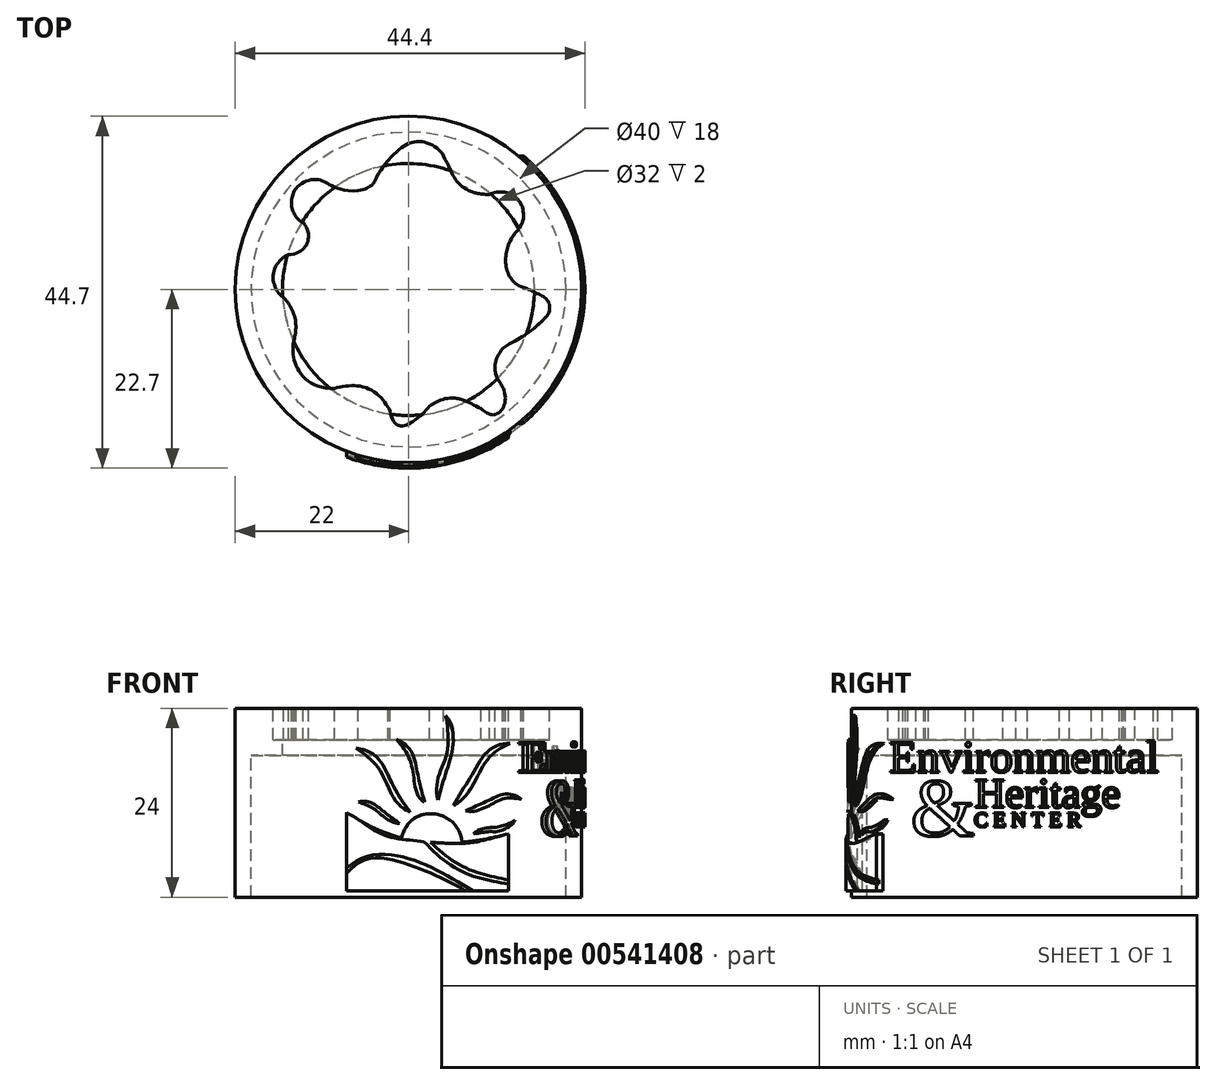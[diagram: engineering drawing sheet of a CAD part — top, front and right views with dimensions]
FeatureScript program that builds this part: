
annotation { "Feature Type Name" : "Feature", "Feature Type Description" : "" }
export const myFeature = defineFeature(function(context is Context, id is Id, definition is map)
    precondition{}
    {
        {
            var Q0;
            Q0=qCreatedBy(makeId("Top.planeOp"),FACE);
            var Q1;
            Q1=qBodyType(qCreatedBy(id+"F1",EDGE),BodyType.WIRE);
            cPlane(context, id + "F0", {"entities" : qUnion([Q0, Q1]), "cplaneType" : CPlaneType.OFFSET, "offset" : 12 * mm, "width" : 150 * mm, "height" : 150 * mm});
        }
        {
            var Q0;
            Q0=qCreatedBy(id+"F0.planeOp",FACE);
            var sketch = newSketch(context, id + "F1", { "sketchPlane" : qUnion([Q0])});
            skCircle(sketch, "E0", {"center": v(0, 0) * mm, "radius": 22 * mm});
            skFitSpline(sketch, "E1", {"points": [v(-14.3, 12.84) * mm, v(-11.44, 13.95) * mm, v(-6.4, 12.53) * mm], "startDerivative": vector(4.46, 5.6) * mm, "endDerivative": vector(16.32, 0.58) * mm});
            skFitSpline(sketch, "E2", {"points": [v(-14.3, 12.84) * mm, v(-14.8, 10.36) * mm, v(-13.38, 8.48) * mm], "startDerivative": vector(-2.91, -3.74) * mm, "endDerivative": vector(4.44, -2.3) * mm});
            skFitSpline(sketch, "E3", {"points": [v(-13.38, 8.48) * mm, v(-12.7, 6.62) * mm, v(-15.26, 4.45) * mm], "startDerivative": vector(2.5, -2.67) * mm, "endDerivative": vector(-9.07, 0.1) * mm});
            skFitSpline(sketch, "E4", {"points": [v(-15.26, 4.45) * mm, v(-17.17, 1.96) * mm, v(-15.87, -1.05) * mm], "startDerivative": vector(-5.88, -2.54) * mm, "endDerivative": vector(5.37, -3.99) * mm});
            skFitSpline(sketch, "E5", {"points": [v(-15.87, -1.05) * mm, v(-14.36, -3.98) * mm, v(-14.54, -6.45) * mm], "startDerivative": vector(4.6, -4.23) * mm, "endDerivative": vector(-1.12, -5.28) * mm});
            skFitSpline(sketch, "E6", {"points": [v(-14.54, -6.45) * mm, v(-14.3, -9.6) * mm, v(-9.38, -12.57) * mm], "startDerivative": vector(-1.49, -4.88) * mm, "endDerivative": vector(14.07, 0.6) * mm});
            skFitSpline(sketch, "E7", {"points": [v(-9.38, -12.57) * mm, v(-5.16, -12.57) * mm, v(-2.36, -15.43) * mm], "startDerivative": vector(7.18, 2.12) * mm, "endDerivative": vector(2.53, -6.19) * mm});
            skFitSpline(sketch, "E8", {"points": [v(-2.36, -15.43) * mm, v(-0.75, -17.32) * mm, v(2.7, -14.82) * mm], "startDerivative": vector(1.67, -9.42) * mm, "endDerivative": vector(5.03, 5.85) * mm});
            skFitSpline(sketch, "E9", {"points": [v(2.7, -14.82) * mm, v(5.45, -13.78) * mm, v(9.22, -15.14) * mm], "startDerivative": vector(4.06, 3.24) * mm, "endDerivative": vector(7.18, -3.93) * mm});
            skFitSpline(sketch, "E10", {"points": [v(9.22, -15.14) * mm, v(11.11, -15.85) * mm, v(12.13, -12.78) * mm], "startDerivative": vector(4.38, -3.77) * mm, "endDerivative": vector(-2.9, 8.35) * mm});
            skFitSpline(sketch, "E11", {"points": [v(12.13, -12.78) * mm, v(11.06, -10.66) * mm, v(11.96, -7.51) * mm], "startDerivative": vector(-1.65, 4.16) * mm, "endDerivative": vector(4.57, 5.25) * mm});
            skFitSpline(sketch, "E12", {"points": [v(11.96, -7.51) * mm, v(14.65, -5.88) * mm, v(17.91, -2.7) * mm], "startDerivative": vector(3.62, 3.57) * mm, "endDerivative": vector(-0.15, 3.1) * mm});
            skFitSpline(sketch, "E13", {"points": [v(17.91, -2.7) * mm, v(16.74, -0.7) * mm, v(14.28, 0.37) * mm], "startDerivative": vector(0.98, 7.59) * mm, "endDerivative": vector(-4.1, 1.2) * mm});
            skFitSpline(sketch, "E14", {"points": [v(14.28, 0.37) * mm, v(12.43, 2.83) * mm, v(12.74, 5.73) * mm], "startDerivative": vector(-6.41, 2.8) * mm, "endDerivative": vector(2.08, 5.38) * mm});
            skFitSpline(sketch, "E15", {"points": [v(12.74, 5.73) * mm, v(14.05, 7.73) * mm, v(14.57, 9.89) * mm], "startDerivative": vector(4.72, 10.1) * mm, "endDerivative": vector(-1.17, 4.74) * mm});
            skFitSpline(sketch, "E16", {"points": [v(14.57, 9.89) * mm, v(13.17, 12.02) * mm, v(10.32, 12.08) * mm], "startDerivative": vector(0.08, 3.85) * mm, "endDerivative": vector(-4.12, -2.28) * mm});
            skFitSpline(sketch, "E17", {"points": [v(10.32, 12.08) * mm, v(6.46, 13.4) * mm, v(4.44, 16.97) * mm], "startDerivative": vector(-9.93, -0.41) * mm, "endDerivative": vector(-5.62, 10.83) * mm});
            skFitSpline(sketch, "E18", {"points": [v(4.44, 16.97) * mm, v(1.52, 18.8) * mm, v(-2.58, 16.4) * mm], "startDerivative": vector(-2.9, 6.35) * mm, "endDerivative": vector(-8.38, -9.56) * mm});
            skFitSpline(sketch, "E19", {"points": [v(-2.58, 16.4) * mm, v(-4.36, 13.61) * mm, v(-6.4, 12.53) * mm], "startDerivative": vector(-9.43, -11.95) * mm, "endDerivative": vector(-8.2, -1.4) * mm});
            skCircle(sketch, "E20", {"center": v(0, 0) * mm, "radius": 20 * mm});
            skSolve(sketch);
        }
        {
            var Q0;
            Q0=qCreatedBy(makeId("Top.planeOp"),FACE);
            cPlane(context, id + "F2", {"entities" : qUnion([Q0]), "cplaneType" : CPlaneType.OFFSET, "offset" : 8 * mm, "width" : 150 * mm, "height" : 150 * mm});
        }
        {
            var Q0;
            Q0=qCreatedBy(id+"F2.planeOp",FACE);
            var sketch = newSketch(context, id + "F3", { "sketchPlane" : qUnion([Q0])});
            skCircle(sketch, "E21", {"center": v(0, 0) * mm, "radius": 20 * mm});
            skCircle(sketch, "E22", {"center": v(0, 0) * mm, "radius": 16 * mm});
            skSolve(sketch);
        }
        {
            var Q0;
            Q0=makeQuery(id+"F1.imprint","IMPRINT",FACE,{"disambiguationData":[TD([[makeQuery(id+"F1.imprint","IMPRINT",EDGE,{"derivedFrom":sQuery(id+"F1.wireOp",EDGE,"E1")}),1.0]])]});
            extrude(context, id + "F4", {"entities" : qUnion([Q0]), "oppositeDirection" : true, "depth" : 4 * mm});
        }
        {
            var Q0;
            Q0=makeQuery(id+"F1.imprint","IMPRINT",FACE,{"disambiguationData":[TD([[makeQuery(id+"F1.imprint","IMPRINT",EDGE,{"derivedFrom":sQuery(id+"F1.wireOp",EDGE,"E0")}),1.0]])]});
            extrude(context, id + "F5", {"entities" : qUnion([Q0]), "operationType" : NewBodyOperationType.ADD, "oppositeDirection" : true, "depth" : 24 * mm});
        }
        {
            var Q0;
            Q0=makeQuery(id+"F3.imprint","IMPRINT",FACE,{"disambiguationData":[TD([[makeQuery(id+"F3.imprint","IMPRINT",EDGE,{"derivedFrom":sQuery(id+"F3.wireOp",EDGE,"E21")}),1.0]])]});
            extrude(context, id + "F6", {"entities" : qUnion([Q0]), "operationType" : NewBodyOperationType.ADD, "oppositeDirection" : true, "depth" : 2 * mm});
        }
        {
            var Q0;
            Q0=qCreatedBy(id+"F0.planeOp",FACE);
            var sketch = newSketch(context, id + "F7", { "sketchPlane" : qUnion([Q0])});
            skCircle(sketch, "E23", {"center": v(0, 0) * mm, "radius": 22.4 * mm});
            skSolve(sketch);
        }
        {
            var Q0;
            Q0=qSketchRegion(id+"F7",true);
            var Q1;
            Q1=qConstructionFilter(qBodyType(qCreatedBy(id+"F7",EDGE),BodyType.WIRE),ConstructionObject.NO);
            extrude(context, id + "F8", {"entities" : qUnion([Q0]), "bodyType" : ToolBodyType.SURFACE, "operationType" : NewBodyOperationType.ADD, "surfaceEntities" : qUnion([Q1]), "oppositeDirection" : true, "depth" : 24 * mm});
        }
        {
            var Q0;
            Q0=qCreatedBy(makeId("Right.planeOp"),FACE);
            var sketch = newSketch(context, id + "F9", { "sketchPlane" : qUnion([Q0])});
            skText(sketch, "E24", { "text": "Environmental", "fontName": "Tinos-Regular.ttf"});
            skText(sketch, "E25", { "text": "Heritage", "fontName": "Tinos-Regular.ttf"});
            skText(sketch, "E26", { "text": "C E N T E R", "fontName": "Tinos-Regular.ttf"});
            skText(sketch, "E27", { "text": "&", "fontName": "Tinos-Regular.ttf"});
            const initialGuessF9  = {"E24": [-0.01718, 0.00388, 1, 0, 0.00415], "E25": [-0.00635, -0.0006, 1, 0, 0.00388], "E26": [-0.00638, -0.00305, 1, 0, 0.0019], "E27": [-0.01444, -0.0042, 1, 0, 0.00757]};
            skSetInitialGuess(sketch, initialGuessF9);
            skSolve(sketch);
        }
        {
            var Q0;
            Q0=qSketchRegion(id+"F9",true);
            var Q1;
            Q1=makeQuery(id+"F8.opExtrude","SWEPT_FACE",FACE,{"disambiguationData":[OSD([sQuery(id+"F7.wireOp",EDGE,"E23")])]});
            var Q2;
            Q2=makeQuery(id+"F5.opExtrude","SWEPT_FACE",FACE,{"disambiguationData":[OSD([sQuery(id+"F1.wireOp",EDGE,"E0")])]});
            extrude(context, id + "F10", {"entities" : qUnion([Q0]), "operationType" : NewBodyOperationType.ADD, "endBound" : BoundingType.UP_TO_SURFACE, "endBoundEntityFace" : qUnion([Q1]), "depth" : 25 * mm, "hasSecondDirection" : true, "secondDirectionBound" : SecondDirectionBoundingType.UP_TO_SURFACE, "secondDirectionOppositeDirection" : false, "secondDirectionBoundEntityFace" : qUnion([Q2]), "secondDirectionDepth" : 25 * mm, "offsetDistance" : 25 * mm});
        }
        {
            var Q0;
            Q0=qCreatedBy(makeId("Front.planeOp"),FACE);
            var sketch = newSketch(context, id + "F11", { "sketchPlane" : qUnion([Q0])});
            skFitSpline(sketch, "E28", {"points": [v(4.72, 11.1) * mm, v(5.15, 5) * mm, v(3.74, 0.35) * mm], "startDerivative": vector(9.25, -10.85) * mm, "endDerivative": vector(-6.86, -24.58) * mm});
            skFitSpline(sketch, "E29", {"points": [v(4.72, 11.1) * mm, v(4.41, 4.9) * mm, v(3.74, 0.35) * mm], "startDerivative": vector(3.34, -19.7) * mm, "endDerivative": vector(3.13, -13.42) * mm});
            skFitSpline(sketch, "E30", {"points": [v(-1.5, 8.04) * mm, v(1.02, 4.33) * mm, v(2.06, 0.08) * mm], "startDerivative": vector(12.14, -4.86) * mm, "endDerivative": vector(3.6, -12.42) * mm});
            skFitSpline(sketch, "E31", {"points": [v(-1.5, 8.04) * mm, v(0.52, 4.19) * mm, v(2.06, 0.08) * mm], "startDerivative": vector(7.17, -8.39) * mm, "endDerivative": vector(7.68, -2.86) * mm});
            skFitSpline(sketch, "E32", {"points": [v(-6.7, 6.92) * mm, v(-2.5, 3.33) * mm, v(0.23, -1.2) * mm], "startDerivative": vector(15.8, -1.39) * mm, "endDerivative": vector(8.45, -10.79) * mm});
            skFitSpline(sketch, "E33", {"points": [v(-6.7, 6.92) * mm, v(-3.04, 3) * mm, v(0.23, -1.2) * mm], "startDerivative": vector(12.7, -8.12) * mm, "endDerivative": vector(11.68, -4.6) * mm});
            skFitSpline(sketch, "E34", {"points": [v(12.9, 7.54) * mm, v(8.27, 3.86) * mm, v(5.73, -0.34) * mm], "startDerivative": vector(-16.28, 0.17) * mm, "endDerivative": vector(-5.04, -10.45) * mm});
            skFitSpline(sketch, "E35", {"points": [v(12.9, 7.54) * mm, v(9.03, 3.9) * mm, v(5.73, -0.34) * mm], "startDerivative": vector(-14.08, -6.51) * mm, "endDerivative": vector(-10.47, -5.32) * mm});
            skFitSpline(sketch, "E36", {"points": [v(7.27, -1.02) * mm, v(10.3, 0.36) * mm, v(14.36, 0.45) * mm], "startDerivative": vector(8.09, 3.76) * mm, "endDerivative": vector(9.5, -7.16) * mm});
            skFitSpline(sketch, "E37", {"points": [v(7.27, -1.02) * mm, v(11.42, 0.27) * mm, v(14.36, 0.45) * mm], "startDerivative": vector(8.44, -2.27) * mm, "endDerivative": vector(8.91, -1.55) * mm});
            skFitSpline(sketch, "E38", {"points": [v(8.29, -3.98) * mm, v(11.06, -3.11) * mm, v(13.55, -2.2) * mm], "startDerivative": vector(4.54, 5.24) * mm, "endDerivative": vector(4.83, 3.04) * mm});
            skFitSpline(sketch, "E39", {"points": [v(8.29, -3.98) * mm, v(11.07, -3.68) * mm, v(13.55, -2.2) * mm], "startDerivative": vector(14.94, 3.04) * mm, "endDerivative": vector(2.67, 5.86) * mm});
            skFitSpline(sketch, "E40", {"points": [v(-6.37, 0.12) * mm, v(-3.47, -0.87) * mm, v(-1.11, -2.63) * mm], "startDerivative": vector(10.1, 1.37) * mm, "endDerivative": vector(5.45, -4.16) * mm});
            skFitSpline(sketch, "E41", {"points": [v(-6.37, 0.12) * mm, v(-3.93, -1.1) * mm, v(-1.11, -2.63) * mm], "startDerivative": vector(7.6, -2.83) * mm, "endDerivative": vector(8.5, -0.9) * mm});
            skFitSpline(sketch, "E42", {"points": [v(-7.86, -1.23) * mm, v(-3.06, -3.79) * mm, v(2, -4.96) * mm], "startDerivative": vector(9.3, -5.74) * mm, "endDerivative": vector(10.6, -1.22) * mm});
            skFitSpline(sketch, "E43", {"points": [v(2, -4.96) * mm, v(6.57, -8.3) * mm, v(12.7, -10.31) * mm], "startDerivative": vector(8.63, -8.7) * mm, "endDerivative": vector(13.46, -2.5) * mm});
            skFitSpline(sketch, "E44", {"points": [v(2.82, -5.02) * mm, v(7.02, -7.88) * mm, v(12.7, -9.8) * mm], "startDerivative": vector(7.75, -7.13) * mm, "endDerivative": vector(11.6, -2.38) * mm});
            skFitSpline(sketch, "E45", {"points": [v(2.82, -5.02) * mm, v(8.2, -4.87) * mm, v(12.7, -3.95) * mm], "startDerivative": vector(11.8, -0.67) * mm, "endDerivative": vector(9.04, 2.33) * mm});
            skFitSpline(sketch, "E46", {"points": [v(-7.86, -8.25) * mm, v(-0.26, -7.54) * mm, v(8.18, -11.18) * mm], "startDerivative": vector(16.62, 9.24) * mm, "endDerivative": vector(16.34, -9.64) * mm});
            skFitSpline(sketch, "E47", {"points": [v(-7.86, -8.96) * mm, v(-0.26, -8.11) * mm, v(7.28, -11.18) * mm], "startDerivative": vector(16.47, 11.33) * mm, "endDerivative": vector(14.69, -7.9) * mm});
            skLineSegment(sketch, "E48", {"start": v(-7.86, -1.23) * mm, "end": v(-7.86, -11.18) * mm});
            skLineSegment(sketch, "E49", {"start": v(-7.86, -11.18) * mm, "end": v(12.7, -11.18) * mm});
            skLineSegment(sketch, "E50", {"start": v(12.7, -3.95) * mm, "end": v(12.7, -11.18) * mm});
            skFitSpline(sketch, "E51", {"points": [v(-0.88, -4.46) * mm, v(3, -1.4) * mm, v(6.78, -5.02) * mm], "startDerivative": vector(3, 13.25) * mm, "endDerivative": vector(0.81, -13.52) * mm});
            skSolve(sketch);
        }
        {
            var Q0;
            Q0 = qSketchRegion(id + "F11", true);
            var Q1;
            Q1=makeQuery(id+"F8.opExtrude","SWEPT_FACE",FACE,{"disambiguationData":[OSD([sQuery(id+"F7.wireOp",EDGE,"E23")])]});
            var Q2;
            {var subQ1=sQuery(id+"F1.wireOp",EDGE,"E0");Q2=makeQuery(id+"F10.boolean.opBoolean","SPLIT",FACE,{"disambiguationData":[TD([makeQuery(id+"F10.opExtrude","SWEPT_FACE",FACE,{"disambiguationData":[OSD([sQuery(id+"F9.wireOp",EDGE,"E24.sketch_text.stroke-0")])]})])],"derivedFrom":makeQuery(id+"F5.opExtrude","SWEPT_FACE",FACE,{"disambiguationData":[OSD([subQ1])]})});}
            extrude(context, id + "F12", {"entities" : qUnion([Q0]), "operationType" : NewBodyOperationType.ADD, "endBound" : BoundingType.UP_TO_SURFACE, "depth" : 25 * mm, "endBoundEntityFace" : qUnion([Q1]), "offsetDistance" : 25 * mm, "hasSecondDirection" : true, "secondDirectionBound" : SecondDirectionBoundingType.UP_TO_SURFACE, "secondDirectionOppositeDirection" : false, "secondDirectionDepth" : 25 * mm, "secondDirectionBoundEntityFace" : qUnion([Q2])});
        }
        {
            var Q0;
            Q0=qCreatedBy(makeId("Front.planeOp"),FACE);
            var sketch = newSketch(context, id + "F13", { "sketchPlane" : qUnion([Q0])});
            skFitSpline(sketch, "E52.0", {"points": [v(-7.86, -8.25) * mm, v(-5.22, -6.79) * mm, v(-0.09, -7.06) * mm, v(5.33, -9.5) * mm, v(8.18, -11.18) * mm]});
            skLineSegment(sketch, "E52.1", {"start": v(-7.86, -1.23) * mm, "end": v(-7.86, -8.25) * mm});
            skFitSpline(sketch, "E52.2", {"points": [v(-7.86, -1.23) * mm, v(-6.3, -2.2) * mm, v(-3.18, -4.07) * mm, v(0.26, -4.76) * mm, v(2, -4.96) * mm]});
            skFitSpline(sketch, "E52.3", {"points": [v(2, -4.96) * mm, v(3.4, -6.36) * mm, v(6.48, -8.59) * mm, v(10.38, -9.88) * mm, v(12.7, -10.31) * mm]});
            skFitSpline(sketch, "E52.4", {"points": [v(2.82, -5.02) * mm, v(4.06, -6.16) * mm, v(6.94, -8.13) * mm, v(10.69, -9.39) * mm, v(12.7, -9.8) * mm]});
            skFitSpline(sketch, "E52.5", {"points": [v(2.82, -5.02) * mm, v(4.86, -5.14) * mm, v(8.1, -5.05) * mm, v(11.25, -4.32) * mm, v(12.7, -3.95) * mm]});
            skLineSegment(sketch, "E52.6", {"start": v(12.7, -3.95) * mm, "end": v(12.7, -11.18) * mm});
            skLineSegment(sketch, "E52.7", {"start": v(-7.86, -11.18) * mm, "end": v(7.28, -11.18) * mm});
            skFitSpline(sketch, "E52.8", {"points": [v(-7.86, -8.96) * mm, v(-5.16, -7.1) * mm, v(-0.18, -7.8) * mm, v(4.8, -9.84) * mm, v(7.28, -11.18) * mm]});
            skLineSegment(sketch, "E53.trimOffspring", {"start": v(-7.86, -8.96) * mm, "end": v(-7.86, -11.18) * mm});
            skLineSegment(sketch, "E54.trimOffspring", {"start": v(8.18, -11.18) * mm, "end": v(12.7, -11.18) * mm});
            skSolve(sketch);
        }
        {
            var Q0;
            Q0=qCreatedBy(id+"F0.planeOp",FACE);
            var sketch = newSketch(context, id + "F14", { "sketchPlane" : qUnion([Q0])});
            skCircle(sketch, "E55", {"center": v(0, 0) * mm, "radius": 22.7 * mm});
            skSolve(sketch);
        }
        {
            var Q0;
            Q0 = qSketchRegion(id + "F14", true);
            var Q1;
            Q1 = qConstructionFilter(qBodyType(qCreatedBy(id + "F14" ,EDGE), BodyType.WIRE), ConstructionObject.NO);
            extrude(context, id + "F15", {"entities" : qUnion([Q0]), "bodyType" : ToolBodyType.SURFACE, "operationType" : NewBodyOperationType.ADD, "surfaceEntities" : qUnion([Q1]), "oppositeDirection" : true, "depth" : 24 * mm, "offsetDistance" : 25 * mm});
        }
        {
            var Q0;
            Q0 = qSketchRegion(id + "F13", true);
            var Q1;
            Q1=makeQuery(id+"F15.opExtrude","SWEPT_FACE",FACE,{"disambiguationData":[OSD([sQuery(id+"F14.wireOp",EDGE,"E55")])]});
            var Q2;
            Q2=makeQuery(id+"F12.opExtrude","CAP_FACE",FACE,{"disambiguationData":[OSD([sQuery(id+"F11.wireOp",EDGE,"E42"),sQuery(id+"F11.wireOp",EDGE,"E45"),sQuery(id+"F11.wireOp",EDGE,"E48"),sQuery(id+"F11.wireOp",EDGE,"E49"),sQuery(id+"F11.wireOp",EDGE,"E50"),sQuery(id+"F11.wireOp",EDGE,"E51")]),OD(0.0)],"isStart":false});
            extrude(context, id + "F16", {"entities" : qUnion([Q0]), "operationType" : NewBodyOperationType.ADD, "endBound" : BoundingType.UP_TO_SURFACE, "depth" : 25 * mm, "endBoundEntityFace" : qUnion([Q1]), "offsetDistance" : 25 * mm, "hasSecondDirection" : true, "secondDirectionBound" : SecondDirectionBoundingType.UP_TO_SURFACE, "secondDirectionOppositeDirection" : false, "secondDirectionDepth" : 25 * mm, "secondDirectionBoundEntityFace" : qUnion([Q2])});
        }
    });
